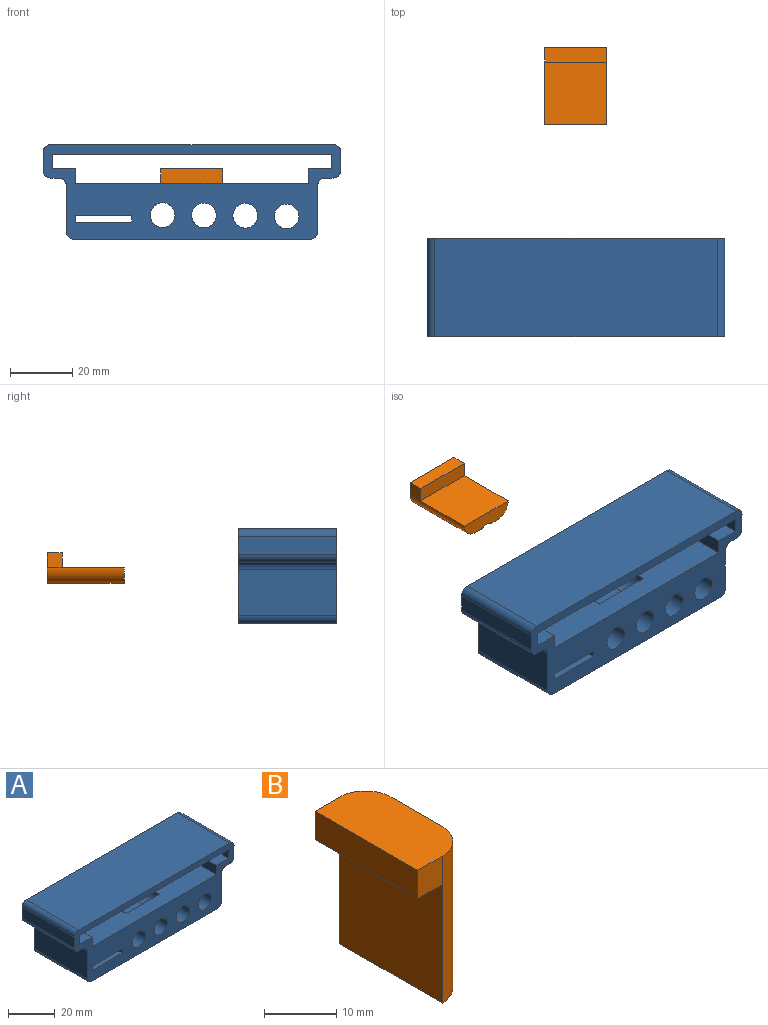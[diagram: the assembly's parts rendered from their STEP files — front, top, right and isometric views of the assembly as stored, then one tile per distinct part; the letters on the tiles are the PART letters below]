
ASSEMBLY  parts=2 mates=1
PART A: 41 faces, bbox 96.1x31.8x30.5 mm
  f0: plane 75.05x31.75mm, normal (0,0,1), area 1888.8mm2, adj f1,f7,f16,f17,f34,f36,f37
  f1: plane 96.1x30.5mm, normal (0,1,0), area 1513.5mm2, adj f0,f2,f3,f4,f5,f6,f7,f8
  f2: plane 31.75x7.5mm, normal (0,0,1), area 238.1mm2, adj f1,f3,f16,f17
  f3: plane 31.75x4.75mm, normal (1,0,0), area 150.8mm2, adj f1,f2,f4,f17
  f4: plane 90.1x31.75mm, normal (0,0,-1), area 2860.7mm2, adj f1,f3,f5,f17
  f5: plane 31.75x4.75mm, normal (-1,0,0.01), area 150.8mm2, adj f1,f4,f6,f17
  f6: plane 31.75x7.5mm, normal (0,0,1), area 238.1mm2, adj f1,f5,f7,f17
  f7: plane 31.75x4.75mm, normal (-1,0,0), area 150.8mm2, adj f0,f1,f6,f17
  f8: plane 31.75x5.75mm, normal (-1,0,0), area 182.6mm2, adj f1,f17,f26,f33
  f9: plane 31.75x2.52mm, normal (0,0,-1), area 80mm2, adj f1,f17,f26,f27
  f10: plane 31.75x14.77mm, normal (-1,0,0), area 468.8mm2, adj f1,f17,f27,f28
  f11: plane 76x31.75mm, normal (0,0,-1), area 2412.9mm2, adj f1,f17,f28,f29
  f12: plane 31.75x14.75mm, normal (1,0,0), area 468.3mm2, adj f1,f17,f29,f30
  f13: plane 31.75x2.5mm, normal (0,0,-1), area 79.3mm2, adj f1,f17,f30,f31
  f14: plane 31.75x5.75mm, normal (1,0,-0.01), area 182.6mm2, adj f1,f17,f31,f32
  f15: plane 91.1x31.75mm, normal (0,0,1), area 2892.5mm2, adj f1,f17,f32,f33
  f16: plane 31.75x4.75mm, normal (1,0,0), area 150.8mm2, adj f0,f1,f2,f17
  f17: plane 96.1x30.5mm, normal (0,-1,0), area 1603.5mm2, adj f0,f2,f3,f4,f5,f6,f7,f8
  f18: plane 31.75x2.14mm, normal (1,0,0), area 68mm2, adj f1,f17,f19,f21
  f19: plane 31.75x18.08mm, normal (0,0,1), area 574mm2, adj f1,f17,f18,f20
  f20: plane 31.75x2.14mm, normal (-1,0,0), area 68mm2, adj f1,f17,f19,f21
  f21: plane 31.75x18.08mm, normal (0,0,-1), area 574mm2, adj f1,f17,f18,f20
  f22: cylinder r=4mm len=31.75mm, axis (0,1,0), area 798mm2, adj f1,f17
  f23: cylinder r=4mm len=31.75mm, axis (0,1,0), area 798mm2, adj f1,f17
  f24: cylinder r=4mm len=31.75mm, axis (0,1,0), area 798mm2, adj f1,f17
  f25: cylinder r=4mm len=31.75mm, axis (0,1,0), area 798mm2, adj f1,f17
  f26: cylinder r=2.5mm len=31.75mm, axis (0,-1,0), area 124.7mm2, adj f1,f8,f9,f17
  f27: cylinder r=2.5mm len=31.75mm, axis (0,-1,0), area 124.4mm2, adj f1,f9,f10,f17
  f28: cylinder r=2.5mm len=31.75mm, axis (0,1,0), area 124.4mm2, adj f1,f10,f11,f17
  f29: cylinder r=2.5mm len=31.75mm, axis (0,-1,0), area 124.7mm2, adj f1,f11,f12,f17
  f30: cylinder r=2.5mm len=31.75mm, axis (0,-1,0), area 124.7mm2, adj f1,f12,f13,f17
  f31: cylinder r=2.5mm len=31.75mm, axis (0,1,0), area 124.1mm2, adj f1,f13,f14,f17
  f32: cylinder r=2.5mm len=31.75mm, axis (0,1,0), area 125.3mm2, adj f1,f14,f15,f17
  f33: cylinder r=2.5mm len=31.75mm, axis (0,1,0), area 124.7mm2, adj f1,f8,f15,f17
  f34: plane 24.7x0.03mm, normal (1,0,0), area 0.8mm2, adj f0,f1,f37,f38
  f35: plane 24.7x10mm, normal (0,0,1), area 243.9mm2, adj f1,f37,f38,f39,f40
  f36: plane 24.7x0.03mm, normal (-1,0,0), area 0.8mm2, adj f0,f1,f37,f39
  f37: plane 20x5.03mm, normal (0,1,0), area 89.9mm2, adj f0,f34,f35,f36,f38,f39
  f38: cylinder r=5mm len=24.7mm, axis (0,-1,0), area 194mm2, adj f1,f34,f35,f37
  f39: cylinder r=5mm len=24.7mm, axis (0,1,0), area 194mm2, adj f1,f35,f36,f37
  f40: sphere r=1mm, area 6.3mm2, adj f35
PART B: 16 faces, bbox 9.8x20x24.8 mm
  f0: plane 24.8x10mm, normal (1,0,0), area 174.2mm2, adj f4,f5,f8,f9,f11,f12,f13
  f1: plane 20x4.8mm, normal (-1,0,0), area 96mm2, adj f2,f5,f6,f7
  f2: plane 20x4.8mm, normal (0,0,-1), area 96mm2, adj f1,f3,f6,f7
  f3: plane 20x20mm, normal (-1,0,0), area 400mm2, adj f2,f4,f8,f9
  f4: plane 20x5mm, normal (0,0,-1), area 87.1mm2, adj f0,f3,f8,f9,f10,f11,f13
  f5: plane 20x9.8mm, normal (0,0,1), area 185.3mm2, adj f0,f1,f6,f7,f8,f9
  f6: plane 4.8x4.8mm, normal (0,-1,0), area 23mm2, adj f1,f2,f5,f9
  f7: plane 4.8x4.8mm, normal (0,1,0), area 23mm2, adj f1,f2,f5,f8
  f8: cylinder r=5mm len=24.8mm, axis (0,0,1), area 194.8mm2, adj f0,f3,f4,f5,f7
  f9: cylinder r=5mm len=24.8mm, axis (0,0,-1), area 194.8mm2, adj f0,f3,f4,f5,f6
  f10: plane 13.4x2mm, normal (1,0,0), area 25.1mm2, adj f4,f11,f12,f13,f14
  f11: cylinder r=2mm len=12.4mm, axis (0,0,1), area 22.2mm2, adj f0,f4,f10,f12
  f12: torus R=2.56mm, axis (1,0,0), area 9.7mm2, adj f0,f10,f11,f13
  f13: cylinder r=2mm len=12.4mm, axis (0,0,1), area 22.2mm2, adj f0,f4,f10,f12
  f14: cylinder r=0.62mm len=1.25mm, axis (1,0,0), area 0.6mm2, adj f10,f15
  f15: plane 1.25x1.25mm, normal (1,0,0), area 1.2mm2, adj f14
PLACE A t=(-13.34,-7.15,-0.14)mm fixed
PLACE B rot(axis=(-0.58,0.58,0.58),120deg) t=(-20.86,15.3,21.32)mm
MATE slider A.f38 <-> B.f8  axis (0,-1,0) through (-15.86,-7.15,26.32)mm
